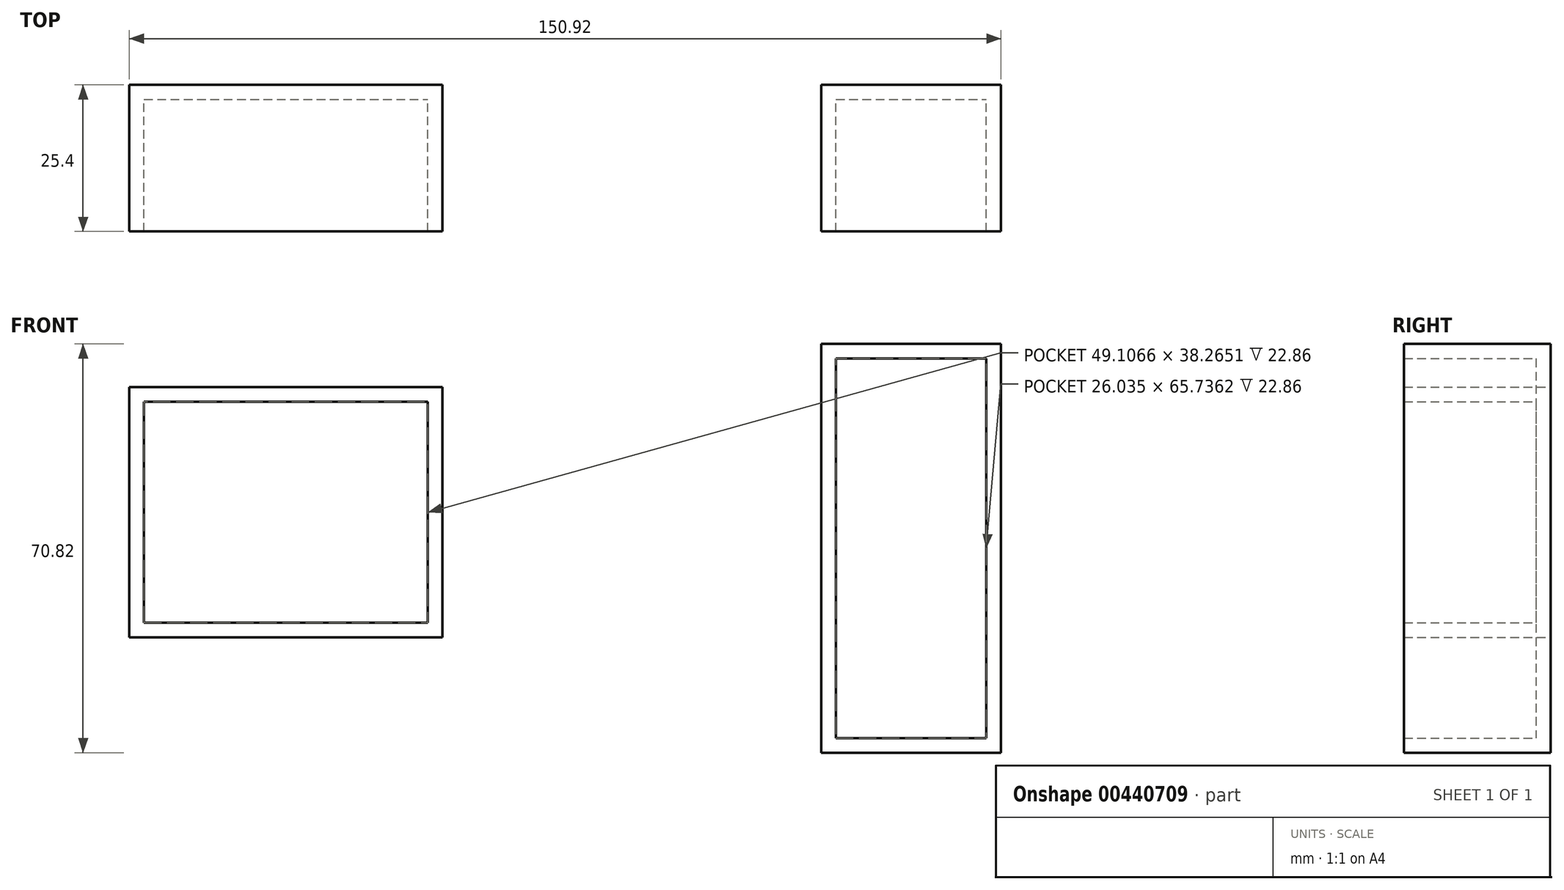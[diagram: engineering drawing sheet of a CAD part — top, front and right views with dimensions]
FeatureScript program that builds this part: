
annotation { "Feature Type Name" : "Feature", "Feature Type Description" : "" }
export const myFeature = defineFeature(function(context is Context, id is Id, definition is map)
    precondition{}
    {
        {
            var Q0;
            Q0=qCreatedBy(makeId("Front.planeOp"),FACE);
            var sketch = newSketch(context, id + "F0", { "sketchPlane" : qUnion([Q0])});
            skLineSegment(sketch, "E0.bottom", {"start": v(-54.19, 95.7) * mm, "end": v(0, 95.7) * mm});
            skLineSegment(sketch, "E0.top", {"start": v(-54.19, 52.35) * mm, "end": v(0, 52.35) * mm});
            skLineSegment(sketch, "E0.left", {"start": v(-54.19, 95.7) * mm, "end": v(-54.19, 52.35) * mm});
            skLineSegment(sketch, "E0.right", {"start": v(0, 95.7) * mm, "end": v(0, 52.35) * mm});
            skLineSegment(sketch, "E1.bottom", {"start": v(65.62, 103.19) * mm, "end": v(96.73, 103.19) * mm});
            skLineSegment(sketch, "E1.top", {"start": v(65.62, 32.37) * mm, "end": v(96.73, 32.37) * mm});
            skLineSegment(sketch, "E1.left", {"start": v(65.62, 103.19) * mm, "end": v(65.62, 32.37) * mm});
            skLineSegment(sketch, "E1.right", {"start": v(96.73, 103.19) * mm, "end": v(96.73, 32.37) * mm});
            skSolve(sketch);
        }
        {
            var Q0;
            Q0 = qSketchRegion(id + "F0", true);
            extrude(context, id + "F1", {"entities" : qUnion([Q0]), "depth" : 25.4 * mm});
        }
        {
            var Q0;
            Q0=makeQuery(id+"F1.opExtrude","CAP_FACE",FACE,{"disambiguationData":[OSD([sQuery(id+"F0.wireOp",EDGE,"E0.bottom"),sQuery(id+"F0.wireOp",EDGE,"E0.top"),sQuery(id+"F0.wireOp",EDGE,"E0.left"),sQuery(id+"F0.wireOp",EDGE,"E0.right")])],"isStart":false});
            shell(context, id + "F2", {"entities" : qUnion([Q0]), "thickness" : 2.54 * mm});
        }
        {
            var Q0;
            Q0=makeQuery(id+"F1.opExtrude","CAP_FACE",FACE,{"disambiguationData":[OSD([sQuery(id+"F0.wireOp",EDGE,"E1.bottom"),sQuery(id+"F0.wireOp",EDGE,"E1.top"),sQuery(id+"F0.wireOp",EDGE,"E1.left"),sQuery(id+"F0.wireOp",EDGE,"E1.right")])],"isStart":false});
            shell(context, id + "F3", {"entities" : qUnion([Q0]), "thickness" : 2.54 * mm});
        }
    });
